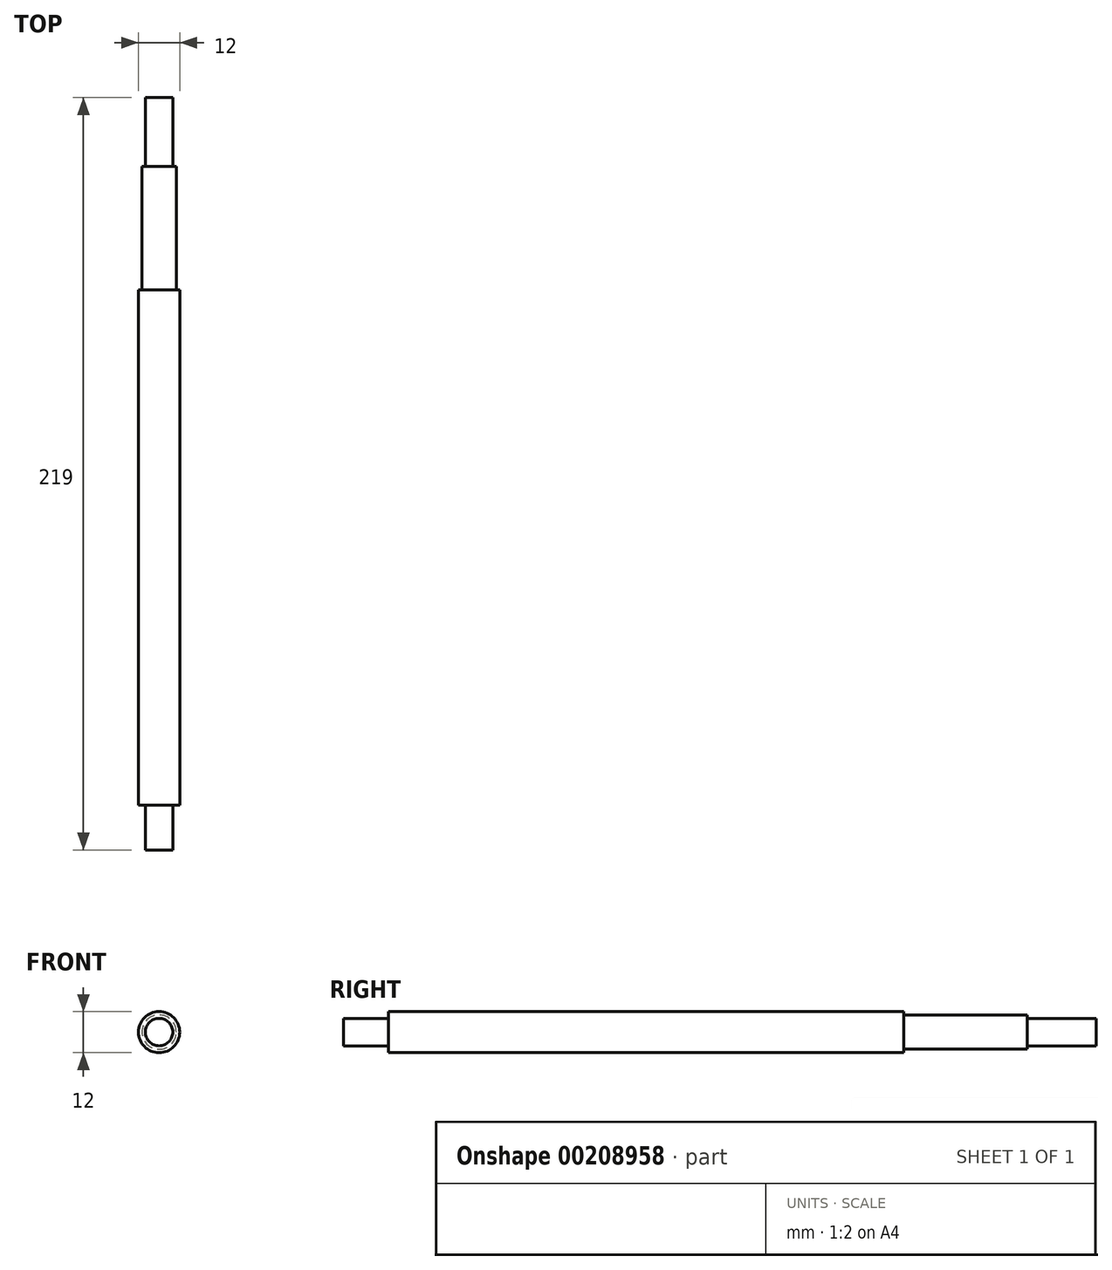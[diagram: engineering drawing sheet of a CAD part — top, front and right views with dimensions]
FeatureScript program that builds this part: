
annotation { "Feature Type Name" : "Feature", "Feature Type Description" : "" }
export const myFeature = defineFeature(function(context is Context, id is Id, definition is map)
    precondition{}
    {
        {
            var Q0;
            Q0=qCreatedBy(makeId("Front.planeOp"),FACE);
            var sketch = newSketch(context, id + "F0", { "sketchPlane" : qUnion([Q0])});
            skCircle(sketch, "E0", {"center": v(0, 0) * mm, "radius": 6 * mm});
            skSolve(sketch);
        }
        {
            var Q0;
            Q0=makeQuery(id+"F0.imprint","IMPRINT",FACE,{"disambiguationData":[TD([[makeQuery(id+"F0.imprint","IMPRINT",EDGE,{"derivedFrom":sQuery(id+"F0.wireOp",EDGE,"E0")}),1.0]])]});
            extrude(context, id + "F1", {"entities" : qUnion([Q0]), "depth" : 150 * mm});
        }
        {
            var Q0;
            Q0=makeQuery(id+"F1.opExtrude","CAP_FACE",FACE,{"disambiguationData":[OSD([sQuery(id+"F0.wireOp",EDGE,"E0")])],"isStart":true});
            var sketch = newSketch(context, id + "F2", { "sketchPlane" : qUnion([Q0])});
            skCircle(sketch, "E1", {"center": v(0, 0) * mm, "radius": 5 * mm});
            skSolve(sketch);
        }
        {
            var Q0;
            Q0=makeQuery(id+"F2.imprint","IMPRINT",FACE,{"disambiguationData":[TD([[makeQuery(id+"F2.imprint","IMPRINT",EDGE,{"derivedFrom":sQuery(id+"F2.wireOp",EDGE,"E1")}),1.0]])]});
            extrude(context, id + "F3", {"entities" : qUnion([Q0]), "operationType" : NewBodyOperationType.ADD, "depth" : 36 * mm});
        }
        {
            var Q0;
            Q0=makeQuery(id+"F3.opExtrude","CAP_FACE",FACE,{"disambiguationData":[OSD([sQuery(id+"F2.wireOp",EDGE,"E1")])],"isStart":false});
            var sketch = newSketch(context, id + "F4", { "sketchPlane" : qUnion([Q0])});
            skCircle(sketch, "E2", {"center": v(0, 0) * mm, "radius": 4 * mm});
            skSolve(sketch);
        }
        {
            var Q0;
            Q0=makeQuery(id+"F4.imprint","IMPRINT",FACE,{"disambiguationData":[TD([[makeQuery(id+"F4.imprint","IMPRINT",EDGE,{"derivedFrom":sQuery(id+"F4.wireOp",EDGE,"E2")}),1.0]])]});
            extrude(context, id + "F5", {"entities" : qUnion([Q0]), "operationType" : NewBodyOperationType.ADD, "depth" : 20 * mm});
        }
        {
            var Q0;
            Q0=makeQuery(id+"F1.opExtrude","CAP_FACE",FACE,{"disambiguationData":[OSD([sQuery(id+"F0.wireOp",EDGE,"E0")])],"isStart":false});
            var sketch = newSketch(context, id + "F6", { "sketchPlane" : qUnion([Q0])});
            skCircle(sketch, "E3", {"center": v(0, 0) * mm, "radius": 4 * mm});
            skSolve(sketch);
        }
        {
            var Q0;
            Q0=makeQuery(id+"F6.imprint","IMPRINT",FACE,{"disambiguationData":[TD([[makeQuery(id+"F6.imprint","IMPRINT",EDGE,{"derivedFrom":sQuery(id+"F6.wireOp",EDGE,"E3")}),1.0]])]});
            extrude(context, id + "F7", {"entities" : qUnion([Q0]), "operationType" : NewBodyOperationType.ADD, "depth" : 13 * mm});
        }
    });
